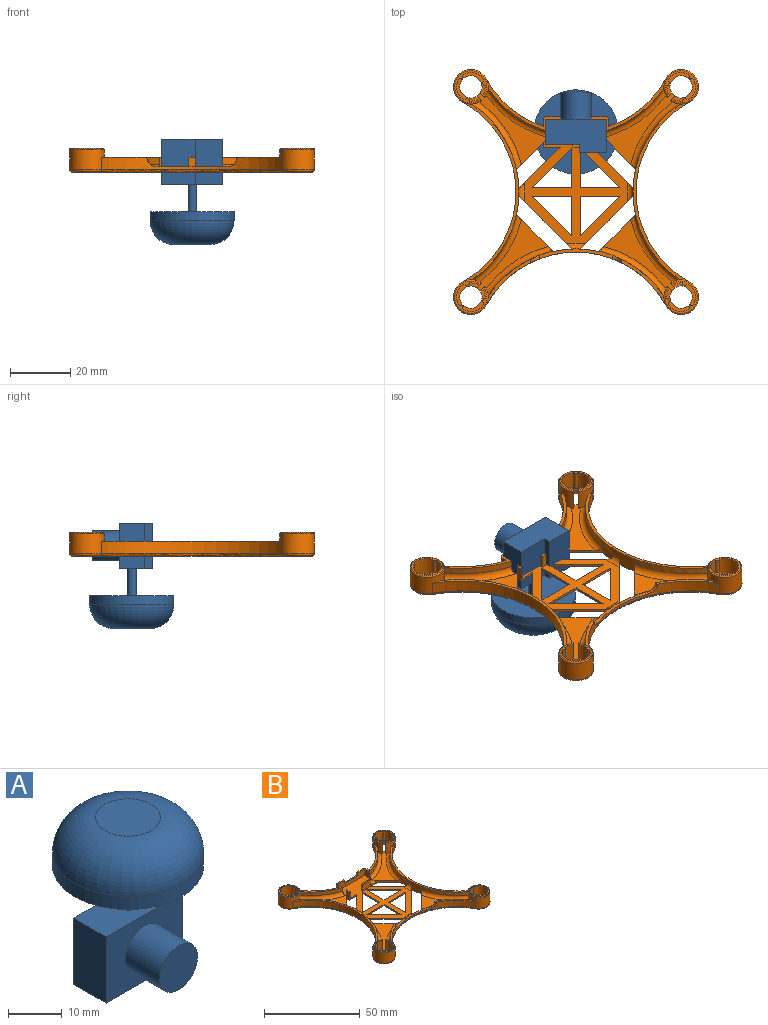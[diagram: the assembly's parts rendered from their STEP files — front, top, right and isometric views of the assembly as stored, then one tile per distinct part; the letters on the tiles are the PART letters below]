
ASSEMBLY  parts=2 mates=1
PART A: 15 faces, bbox 28x28x35 mm
  f0: cylinder r=1.5mm len=9mm, axis (0,0,-1), area 84.8mm2, adj f7,f12
  f1: plane 15x11mm, normal (0,1,0), area 165mm2, adj f2,f6,f7,f8
  f2: plane 15x8.5mm, normal (-1,0,0), area 127.5mm2, adj f1,f3,f7,f8
  f3: plane 20x15mm, normal (0,-1,0), area 221.5mm2, adj f2,f4,f7,f8,f9
  f4: plane 15x11mm, normal (1,0,0), area 165mm2, adj f3,f5,f7,f8
  f5: plane 15x9mm, normal (0,1,0), area 135mm2, adj f4,f6,f7,f8
  f6: plane 15x2.5mm, normal (-1,0,0), area 37.5mm2, adj f1,f5,f7,f8
  f7: plane 20x11mm, normal (0,0,1), area 185.4mm2, adj f0,f1,f2,f3,f4,f5,f6
  f8: plane 20x11mm, normal (0,0,-1), area 192.5mm2, adj f1,f2,f3,f4,f5,f6
  f9: cylinder r=5mm len=10mm, axis (0,1,0), area 282.7mm2, adj f3,f10
  f10: plane 10x10mm, normal (0,-1,0), area 78.5mm2, adj f9
  f11: cylinder r=14mm len=28mm, axis (0,0,-1), area 263.9mm2, adj f12,f14
  f12: plane 28x28mm, normal (0,0,-1), area 608.7mm2, adj f0,f11
  f13: plane 12x12mm, normal (0,0,1), area 113.1mm2, adj f14
  f14: torus R=6mm, axis (0,0,1), area 875.9mm2, adj f11,f13
PART B: 151 faces, bbox 82.5x82.5x8 mm
  f0: plane 79.5x58.77mm, normal (0,0,-1), area 1143.6mm2, adj f9,f15,f18,f19,f23,f25,f26,f44
  f1: plane 32.2x32.2mm, normal (0,0,-1), area 261.6mm2, adj f74,f78,f137,f140,f142
  f2: cylinder r=35.14mm len=15.22mm, axis (0,0,-1), area 42.7mm2, adj f46,f60,f65,f132
  f3: cylinder r=35.14mm len=6.27mm, axis (0,0,-1), area 12.7mm2, adj f48,f51,f133,f142
  f4: cylinder r=35.14mm len=6.27mm, axis (0,0,-1), area 12.7mm2, adj f74,f77,f133,f142
  f5: plane 15.4x14.96mm, normal (0,0,1), area 19.5mm2, adj f47,f50,f72,f134
  f6: plane 24.96x17.31mm, normal (0,0,1), area 31.4mm2, adj f7,f8,f12,f13,f20,f117,f120,f130
  f7: plane 19.6x4mm, normal (0,1,0), area 58.4mm2, adj f6,f16,f129,f130,f131,f139,f143,f144
  f8: plane 20x4.2mm, normal (0,-1,0), area 64mm2, adj f6,f11,f16,f119,f120,f129,f130,f131
  f9: plane 9.02x9.02mm, normal (0.71,-0.71,0), area 11.2mm2, adj f0,f11,f21,f40,f124
  f10: cylinder r=34.14mm len=19.16mm, axis (0,0,-1), area 102.2mm2, adj f16,f97,f118,f136
  f11: plane 65.86x50.07mm, normal (0,0,1), area 847.5mm2, adj f8,f9,f14,f15,f18,f19,f20,f23
  f12: cylinder r=34.14mm len=19.16mm, axis (0,0,-1), area 102.2mm2, adj f6,f20,f117,f150
  f13: cylinder r=35.14mm len=19.26mm, axis (0,0,-1), area 53.7mm2, adj f6,f14,f20,f120
  f14: torus R=37.14mm, axis (0,0,1), area 76.8mm2, adj f11,f13,f20,f120
  f15: plane 14.51x14.51mm, normal (0.71,0.71,0), area 22.3mm2, adj f0,f11,f73,f92,f114,f125,f127,f128
  f16: plane 24.96x17.31mm, normal (0,0,1), area 31.4mm2, adj f7,f8,f10,f22,f97,f118,f119,f131
  f17: cylinder r=4.75mm len=7.12mm, axis (0,0,-1), area 50.7mm2, adj f32,f36,f37,f38
  f18: plane 13.05x0.8mm, normal (0,1,0), area 10.4mm2, adj f0,f11,f19,f23
  f19: plane 13.05x13.05mm, normal (0.71,-0.71,0), area 14.8mm2, adj f0,f11,f18,f23
  f20: cylinder r=5.75mm len=11.5mm, axis (0,0,-1), area 201.8mm2, adj f6,f11,f12,f13,f14,f21,f24,f28
  f21: cylinder r=35.14mm len=58.52mm, axis (0,0,-1), area 187.6mm2, adj f9,f20,f25,f35,f40,f41,f46,f48
  f22: cylinder r=35.14mm len=19.26mm, axis (0,0,-1), area 53.7mm2, adj f16,f97,f112,f119
  f23: plane 13.05x0.8mm, normal (-1,0,0), area 10.4mm2, adj f0,f11,f18,f19
  f24: cylinder r=34.14mm len=59.91mm, axis (0,0,-1), area 292.3mm2, adj f20,f35,f46,f147
  f25: plane 13.71x13.71mm, normal (-0.71,0.71,0), area 16.7mm2, adj f0,f11,f21,f41,f116
  f26: cylinder r=3.75mm len=7.5mm, axis (0,0,-1), area 45.3mm2, adj f0,f11,f28,f34,f36
  f27: plane 32.2x32.2mm, normal (0,0,-1), area 261.6mm2, adj f48,f52,f142,f145,f147
  f28: plane 7.22x1.46mm, normal (0.71,0.71,0), area 8.5mm2, adj f11,f20,f26,f29,f36,f38,f39
  f29: cylinder r=4.75mm len=6mm, axis (0,0,-1), area 20.8mm2, adj f28,f30,f36,f38
  f30: cylinder r=0.79mm len=6mm, axis (0,0,-1), area 11.8mm2, adj f29,f31,f36,f38
  f31: cylinder r=4.75mm len=7.12mm, axis (0,0,-1), area 50.7mm2, adj f30,f36,f37,f38
  f32: cylinder r=0.79mm len=6mm, axis (0,0,-1), area 11.8mm2, adj f17,f33,f36,f38
  f33: cylinder r=4.75mm len=6mm, axis (0,0,-1), area 20.8mm2, adj f32,f34,f36,f38
  f34: plane 7.22x1.46mm, normal (-0.71,-0.71,0), area 8.5mm2, adj f11,f20,f26,f33,f36,f38,f39
  f35: plane 59.91x18.76mm, normal (0,0,1), area 70mm2, adj f20,f21,f24,f46
  f36: plane 9.5x9.5mm, normal (0,0,1), area 23.2mm2, adj f17,f26,f28,f29,f30,f31,f32,f33
  f37: cylinder r=0.79mm len=6mm, axis (0,0,-1), area 11.8mm2, adj f17,f31,f36,f38
  f38: plane 10.7x10.7mm, normal (0,0,1), area 20.1mm2, adj f17,f28,f29,f30,f31,f32,f33,f34
  f39: torus R=5.35mm, axis (0,0,1), area 21.2mm2, adj f20,f28,f34,f38
  f40: torus R=37.14mm, axis (0,0,1), area 82.8mm2, adj f9,f11,f20,f21
  f41: torus R=37.14mm, axis (0,0,1), area 12.3mm2, adj f11,f21,f25,f51
  f42: cylinder r=4.75mm len=7.12mm, axis (0,0,-1), area 50.7mm2, adj f57,f61,f62,f63
  f43: plane 23.73x23.73mm, normal (0,0,1), area 124mm2, adj f46,f48,f52,f53,f59,f65,f67
  f44: plane 13.05x0.8mm, normal (-1,0,0), area 10.4mm2, adj f0,f11,f45,f49
  f45: plane 13.05x13.05mm, normal (0.71,0.71,0), area 14.8mm2, adj f0,f11,f44,f49
  f46: cylinder r=5.75mm len=11.5mm, axis (0,0,-1), area 201.8mm2, adj f2,f21,f24,f35,f43,f50,f53,f59
  f47: cylinder r=35.14mm len=15.22mm, axis (0,0,-1), area 42.7mm2, adj f5,f72,f93,f134
  f48: plane 12.27x12.27mm, normal (0.71,0.71,0), area 15.9mm2, adj f3,f21,f27,f43,f65,f67,f133
  f49: plane 13.05x0.8mm, normal (0,-1,0), area 10.4mm2, adj f0,f11,f44,f45
  f50: cylinder r=34.14mm len=59.91mm, axis (0,0,-1), area 203.4mm2, adj f5,f46,f60,f72,f132,f133,f134,f142
  f51: plane 17.75x17.75mm, normal (-0.71,-0.71,0), area 22.3mm2, adj f0,f3,f11,f21,f41,f66,f133
  f52: cylinder r=3.75mm len=7.5mm, axis (0,0,-1), area 45.3mm2, adj f27,f43,f53,f59,f61
  f53: plane 7.22x1.46mm, normal (-0.71,0.71,0), area 8.5mm2, adj f43,f46,f52,f54,f61,f63,f64
  f54: cylinder r=4.75mm len=6mm, axis (0,0,-1), area 20.8mm2, adj f53,f55,f61,f63
  f55: cylinder r=0.79mm len=6mm, axis (0,0,-1), area 11.8mm2, adj f54,f56,f61,f63
  f56: cylinder r=4.75mm len=7.12mm, axis (0,0,-1), area 50.7mm2, adj f55,f61,f62,f63
  f57: cylinder r=0.79mm len=6mm, axis (0,0,-1), area 11.8mm2, adj f42,f58,f61,f63
  f58: cylinder r=4.75mm len=6mm, axis (0,0,-1), area 20.8mm2, adj f57,f59,f61,f63
  f59: plane 7.22x1.46mm, normal (0.71,-0.71,0), area 8.5mm2, adj f43,f46,f52,f58,f61,f63,f64
  f60: plane 15.4x14.96mm, normal (0,0,1), area 19.5mm2, adj f2,f46,f50,f132
  f61: plane 9.5x9.5mm, normal (0,0,1), area 23.2mm2, adj f42,f52,f53,f54,f55,f56,f57,f58
  f62: cylinder r=0.79mm len=6mm, axis (0,0,-1), area 11.8mm2, adj f42,f56,f61,f63
  f63: plane 10.7x10.7mm, normal (0,0,1), area 20.1mm2, adj f42,f53,f54,f55,f56,f57,f58,f59
  f64: torus R=5.35mm, axis (0,0,1), area 21.2mm2, adj f46,f53,f59,f63
  f65: torus R=37.14mm, axis (0,0,1), area 77.8mm2, adj f2,f43,f46,f48,f132,f133
  f66: torus R=37.14mm, axis (0,0,1), area 10.2mm2, adj f11,f51,f77,f133
  f67: torus R=37.14mm, axis (0,0,1), area 82.8mm2, adj f21,f43,f46,f48
  f68: cylinder r=4.75mm len=7.12mm, axis (0,0,-1), area 50.7mm2, adj f83,f87,f88,f89
  f69: plane 23.73x23.73mm, normal (0,0,1), area 124mm2, adj f72,f74,f78,f79,f85,f91,f93
  f70: plane 13.05x0.8mm, normal (0,-1,0), area 10.4mm2, adj f0,f11,f71,f75
  f71: plane 13.05x13.05mm, normal (-0.71,0.71,0), area 14.8mm2, adj f0,f11,f70,f75
  f72: cylinder r=5.75mm len=11.5mm, axis (0,0,-1), area 201.8mm2, adj f5,f47,f50,f69,f73,f76,f79,f85
  f73: cylinder r=35.14mm len=58.52mm, axis (0,0,-1), area 187.6mm2, adj f15,f72,f74,f77,f86,f91,f92,f97
  f74: plane 12.27x12.27mm, normal (-0.71,0.71,0), area 15.9mm2, adj f1,f4,f69,f73,f91,f93,f133
  f75: plane 13.05x0.8mm, normal (1,0,0), area 10.4mm2, adj f0,f11,f70,f71
  f76: cylinder r=34.14mm len=59.91mm, axis (0,0,-1), area 292.3mm2, adj f72,f86,f97,f137
  f77: plane 17.75x17.75mm, normal (0.71,-0.71,0), area 22.3mm2, adj f0,f4,f11,f66,f73,f92,f133
  f78: cylinder r=3.75mm len=7.5mm, axis (0,0,-1), area 45.3mm2, adj f1,f69,f79,f85,f87
  f79: plane 7.22x1.46mm, normal (-0.71,-0.71,0), area 8.5mm2, adj f69,f72,f78,f80,f87,f89,f90
  f80: cylinder r=4.75mm len=6mm, axis (0,0,-1), area 20.8mm2, adj f79,f81,f87,f89
  f81: cylinder r=0.79mm len=6mm, axis (0,0,-1), area 11.8mm2, adj f80,f82,f87,f89
  f82: cylinder r=4.75mm len=7.12mm, axis (0,0,-1), area 50.7mm2, adj f81,f87,f88,f89
  f83: cylinder r=0.79mm len=6mm, axis (0,0,-1), area 11.8mm2, adj f68,f84,f87,f89
  f84: cylinder r=4.75mm len=6mm, axis (0,0,-1), area 20.8mm2, adj f83,f85,f87,f89
  f85: plane 7.22x1.46mm, normal (0.71,0.71,0), area 8.5mm2, adj f69,f72,f78,f84,f87,f89,f90
  f86: plane 59.91x18.76mm, normal (0,0,1), area 70mm2, adj f72,f73,f76,f97
  f87: plane 9.5x9.5mm, normal (0,0,1), area 23.2mm2, adj f68,f78,f79,f80,f81,f82,f83,f84
  f88: cylinder r=0.79mm len=6mm, axis (0,0,-1), area 11.8mm2, adj f68,f82,f87,f89
  f89: plane 10.7x10.7mm, normal (0,0,1), area 20.1mm2, adj f68,f79,f80,f81,f82,f83,f84,f85
  f90: torus R=5.35mm, axis (0,0,1), area 21.2mm2, adj f72,f79,f85,f89
  f91: torus R=37.14mm, axis (0,0,1), area 82.8mm2, adj f69,f72,f73,f74
  f92: torus R=37.14mm, axis (0,0,1), area 12.3mm2, adj f11,f15,f73,f77
  f93: torus R=37.14mm, axis (0,0,1), area 77.8mm2, adj f47,f69,f72,f74,f133,f134
  f94: cylinder r=4.75mm len=7.12mm, axis (0,0,-1), area 50.7mm2, adj f105,f108,f109,f110
  f95: plane 13.05x0.8mm, normal (1,0,0), area 10.4mm2, adj f0,f11,f96,f99
  f96: plane 13.05x13.05mm, normal (-0.71,-0.71,0), area 14.8mm2, adj f0,f11,f95,f99
  f97: cylinder r=5.75mm len=11.5mm, axis (0,0,-1), area 201.8mm2, adj f10,f11,f16,f22,f73,f76,f86,f101
  f98: plane 9.82x9.82mm, normal (-0.71,-0.71,0), area 12.1mm2, adj f0,f11,f73,f113,f115
  f99: plane 13.05x0.8mm, normal (0,1,0), area 10.4mm2, adj f0,f11,f95,f96
  f100: cylinder r=3.75mm len=7.5mm, axis (0,0,-1), area 45.3mm2, adj f0,f11,f101,f107,f108
  f101: plane 7.22x1.46mm, normal (0.71,-0.71,0), area 8.5mm2, adj f11,f97,f100,f102,f108,f110,f111
  f102: cylinder r=4.75mm len=6mm, axis (0,0,-1), area 20.8mm2, adj f101,f103,f108,f110
  f103: cylinder r=0.79mm len=6mm, axis (0,0,-1), area 11.8mm2, adj f102,f104,f108,f110
  f104: cylinder r=4.75mm len=7.12mm, axis (0,0,-1), area 50.7mm2, adj f103,f108,f109,f110
  f105: cylinder r=0.79mm len=6mm, axis (0,0,-1), area 11.8mm2, adj f94,f106,f108,f110
  f106: cylinder r=4.75mm len=6mm, axis (0,0,-1), area 20.8mm2, adj f105,f107,f108,f110
  f107: plane 7.22x1.46mm, normal (-0.71,0.71,0), area 8.5mm2, adj f11,f97,f100,f106,f108,f110,f111
  f108: plane 9.5x9.5mm, normal (0,0,1), area 23.2mm2, adj f94,f100,f101,f102,f103,f104,f105,f106
  f109: cylinder r=0.79mm len=6mm, axis (0,0,-1), area 11.8mm2, adj f94,f104,f108,f110
  f110: plane 10.7x10.7mm, normal (0,0,1), area 20.1mm2, adj f94,f101,f102,f103,f104,f105,f106,f107
  f111: torus R=5.35mm, axis (0,0,1), area 21.2mm2, adj f97,f101,f107,f110
  f112: torus R=37.14mm, axis (0,0,1), area 76.8mm2, adj f11,f22,f97,f119
  f113: torus R=37.14mm, axis (0,0,1), area 82.8mm2, adj f11,f73,f97,f98
  f114: plane 5.48x0.8mm, normal (0,-1,0), area 4.4mm2, adj f0,f11,f15,f115
  f115: plane 1.59x0.8mm, normal (1,0,0), area 1.3mm2, adj f0,f11,f98,f114
  f116: plane 5.48x5mm, normal (0,-1,0), area 7.7mm2, adj f0,f11,f25,f121,f122,f124
  f117: plane 4x2.32mm, normal (-1,0,0), area 9.3mm2, adj f6,f12,f144,f148
  f118: plane 4x2.32mm, normal (1,0,0), area 9.3mm2, adj f10,f16,f138,f139
  f119: plane 5.91x4.2mm, normal (-1,0,0), area 17mm2, adj f8,f11,f16,f22,f112
  f120: plane 5.91x4.2mm, normal (1,0,0), area 17mm2, adj f6,f8,f11,f13,f14
  f121: plane 2.39x0.8mm, normal (0,0,1), area 1.6mm2, adj f116,f122,f123,f124
  f122: plane 4.2x2.39mm, normal (1,0,0), area 10mm2, adj f11,f116,f121,f123
  f123: plane 4.2x0.8mm, normal (-0.71,0.71,0), area 4.8mm2, adj f11,f121,f122,f124
  f124: plane 5x1.59mm, normal (-1,0,0), area 7.9mm2, adj f0,f9,f116,f121,f123
  f125: plane 6.32x0.8mm, normal (0,0,1), area 4.7mm2, adj f15,f126,f127,f128
  f126: plane 4.2x0.8mm, normal (-1,0,0), area 3.4mm2, adj f11,f125,f127,f128
  f127: plane 5.52x4.2mm, normal (0,1,0), area 23.2mm2, adj f11,f15,f125,f126
  f128: plane 6.32x4.2mm, normal (0,-1,0), area 26.5mm2, adj f11,f15,f125,f126
  f129: plane 10x0.8mm, normal (0,0,1), area 8mm2, adj f7,f8,f130,f131
  f130: plane 2x0.8mm, normal (1,0,0), area 1.6mm2, adj f6,f7,f8,f129
  f131: plane 2x0.8mm, normal (-1,0,0), area 1.6mm2, adj f7,f8,f16,f129
  f132: cylinder r=3mm len=3mm, axis (0,-1,0), area 5.4mm2, adj f2,f50,f60,f65,f133
  f133: plane 24x3.35mm, normal (0,0,1), area 26.5mm2, adj f3,f4,f48,f50,f51,f65,f66,f74
  f134: cylinder r=3mm len=3mm, axis (0,-1,0), area 5.4mm2, adj f5,f47,f50,f93,f133
  f135: torus R=4.75mm, axis (0,0,1), area 31.4mm2, adj f0,f97,f136,f137
  f136: torus R=35.14mm, axis (0,0,1), area 41.4mm2, adj f0,f10,f135,f138
  f137: torus R=35.14mm, axis (0,0,1), area 116mm2, adj f0,f1,f73,f76,f135,f140
  f138: cylinder r=1mm len=3.68mm, axis (0,1,0), area 4.4mm2, adj f0,f118,f136,f141
  f139: cylinder r=1mm len=4mm, axis (0,0,1), area 6.3mm2, adj f7,f16,f118,f141
  f140: torus R=4.75mm, axis (0,0,1), area 31.4mm2, adj f1,f72,f137,f142
  f141: sphere r=1mm, area 1.6mm2, adj f138,f139,f143
  f142: torus R=35.14mm, axis (0,0,1), area 116mm2, adj f0,f1,f3,f4,f27,f50,f140,f145
  f143: cylinder r=1mm len=19.6mm, axis (-1,0,0), area 30.8mm2, adj f0,f7,f141,f146
  f144: cylinder r=1mm len=4mm, axis (0,0,-1), area 6.3mm2, adj f6,f7,f117,f146
  f145: torus R=4.75mm, axis (0,0,1), area 31.4mm2, adj f27,f46,f142,f147
  f146: sphere r=1mm, area 1.6mm2, adj f143,f144,f148
  f147: torus R=35.14mm, axis (0,0,1), area 116mm2, adj f0,f21,f24,f27,f145,f149
  f148: cylinder r=1mm len=3.68mm, axis (0,-1,0), area 4.4mm2, adj f0,f117,f146,f150
  f149: torus R=4.75mm, axis (0,0,1), area 31.4mm2, adj f0,f20,f147,f150
  f150: torus R=35.14mm, axis (0,0,1), area 41.4mm2, adj f0,f12,f148,f149
PLACE A rot(axis=(1,0,0),180deg) t=(-8.48,16.95,-27.88)mm
PLACE B t=(1.52,-7.32,-38.88)mm
MATE planar A.f9 <-> B.f8  axis (0,1,0) through (1.52,16.95,-35.38)mm
